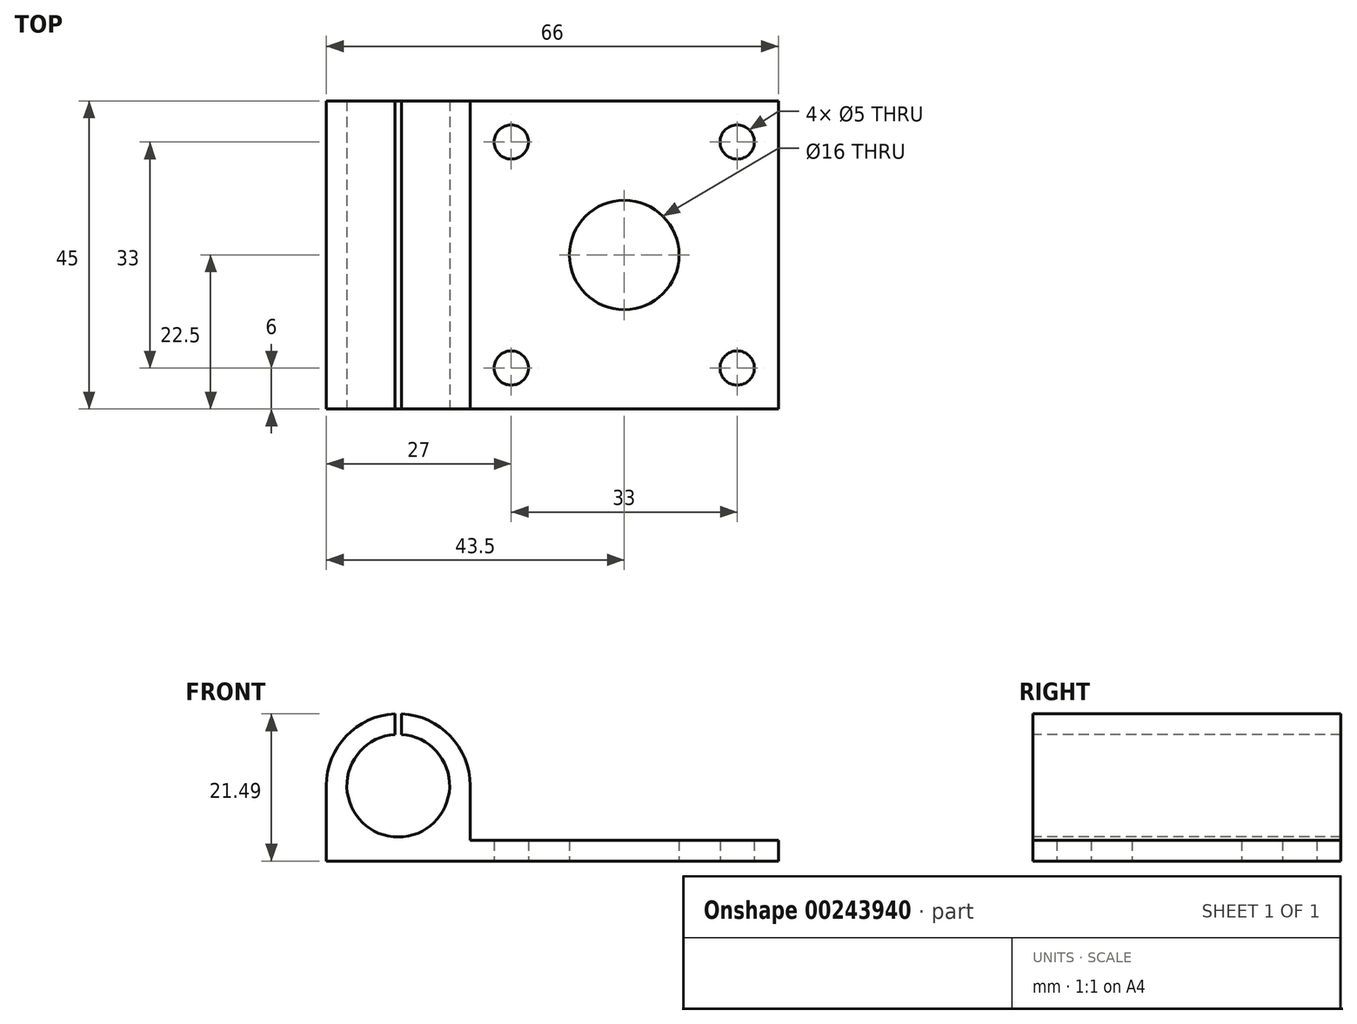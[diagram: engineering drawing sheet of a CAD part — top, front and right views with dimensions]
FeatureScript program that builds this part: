
annotation { "Feature Type Name" : "Feature", "Feature Type Description" : "" }
export const myFeature = defineFeature(function(context is Context, id is Id, definition is map)
    precondition{}
    {
        {
            var Q0;
            Q0=qCreatedBy(makeId("Front.planeOp"),FACE);
            var sketch = newSketch(context, id + "F0", { "sketchPlane" : qUnion([Q0])});
            skArc(sketch, "E0", {"start": v(-11, 18.48) * mm, "mid": v(-10.5, 3.5) * mm, "end": v(-10, 18.48) * mm});
            skArc(sketch, "E1", {"start": v(-11, 21.49) * mm, "mid": v(-18.1, 18.25) * mm, "end": v(-21, 11) * mm});
            skLineSegment(sketch, "E2.0", {"start": v(-21, 0) * mm, "end": v(-21, 11) * mm});
            skLineSegment(sketch, "E3.0", {"start": v(45, 3) * mm, "end": v(0, 3) * mm});
            skLineSegment(sketch, "E4.trimOffspring", {"start": v(-11, 18.48) * mm, "end": v(-11, 21.5) * mm});
            skLineSegment(sketch, "E5.trimOffspring", {"start": v(-10, 18.48) * mm, "end": v(-10, 21.5) * mm});
            skArc(sketch, "E6.trimOffspring", {"start": v(0, 11) * mm, "mid": v(-2.9, 18.25) * mm, "end": v(-10, 21.49) * mm});
            skLineSegment(sketch, "E7", {"start": v(-21, 0) * mm, "end": v(45, 0) * mm});
            skPoint(sketch, "E8.endSnap0", {"position": v(-10.5, 3.5) * mm});
            skLineSegment(sketch, "E9.0", {"start": v(0, 11) * mm, "end": v(0, 3) * mm});
            skLineSegment(sketch, "E10", {"start": v(0, 3) * mm, "end": v(0, 0) * mm, "construction": true});
            skLineSegment(sketch, "E11.0", {"start": v(45, 3) * mm, "end": v(45, 0) * mm});
            skSolve(sketch);
        }
        {
            var Q0;
            {var subQ1=sQuery(id+"F0.wireOp",EDGE,"E0");Q0=makeQuery(id+"F0.imprint","IMPRINT",FACE,{"disambiguationData":[TD([[makeQuery(id+"F0.imprint","IMPRINT",EDGE,{"derivedFrom":subQ1}),-1.0]])]});}
            extrude(context, id + "F1", {"entities" : qUnion([Q0]), "oppositeDirection" : true, "depth" : 45 * mm});
        }
        {
            var Q0;
            Q0=qCreatedBy(makeId("Top.planeOp"),FACE);
            var sketch = newSketch(context, id + "F2", { "sketchPlane" : qUnion([Q0])});
            skLineSegment(sketch, "E12", {"start": v(0, 0) * mm, "end": v(0, 22.5) * mm, "construction": true});
            skLineSegment(sketch, "E13", {"start": v(0, 22.5) * mm, "end": v(22.5, 22.5) * mm, "construction": true});
            skLineSegment(sketch, "E14", {"start": v(0, 0) * mm, "end": v(45, 0) * mm, "construction": true});
            skLineSegment(sketch, "E15", {"start": v(45, 0) * mm, "end": v(45, 45) * mm, "construction": true});
            skLineSegment(sketch, "E16", {"start": v(45, 45) * mm, "end": v(0, 45) * mm, "construction": true});
            skLineSegment(sketch, "E17.0", {"start": v(6, 6) * mm, "end": v(6, 39) * mm, "construction": true});
            skLineSegment(sketch, "E18.0", {"start": v(6, 6) * mm, "end": v(39, 6) * mm, "construction": true});
            skLineSegment(sketch, "E19.0", {"start": v(39, 6) * mm, "end": v(39, 39) * mm, "construction": true});
            skLineSegment(sketch, "E20.0", {"start": v(39, 39) * mm, "end": v(6, 39) * mm, "construction": true});
            skCircle(sketch, "E21", {"center": v(22.5, 22.5) * mm, "radius": 8 * mm});
            skCircle(sketch, "E22", {"center": v(6, 6) * mm, "radius": 2.5 * mm});
            skCircle(sketch, "E23", {"center": v(39, 6) * mm, "radius": 2.5 * mm});
            skCircle(sketch, "E24", {"center": v(6, 39) * mm, "radius": 2.5 * mm});
            skCircle(sketch, "E25", {"center": v(39, 39) * mm, "radius": 2.5 * mm});
            skSolve(sketch);
        }
        {
            var Q0;
            Q0=makeQuery(id+"F2.imprint","IMPRINT",FACE,{"disambiguationData":[TD([[makeQuery(id+"F2.imprint","IMPRINT",EDGE,{"derivedFrom":sQuery(id+"F2.wireOp",EDGE,"E21")}),1.0]])]});
            var Q1;
            Q1=makeQuery(id+"F2.imprint","IMPRINT",FACE,{"disambiguationData":[TD([[makeQuery(id+"F2.imprint","IMPRINT",EDGE,{"derivedFrom":sQuery(id+"F2.wireOp",EDGE,"E24")}),1.0]])]});
            var Q2;
            Q2=makeQuery(id+"F2.imprint","IMPRINT",FACE,{"disambiguationData":[TD([[makeQuery(id+"F2.imprint","IMPRINT",EDGE,{"derivedFrom":sQuery(id+"F2.wireOp",EDGE,"E25")}),1.0]])]});
            var Q3;
            Q3=makeQuery(id+"F2.imprint","IMPRINT",FACE,{"disambiguationData":[TD([[makeQuery(id+"F2.imprint","IMPRINT",EDGE,{"derivedFrom":sQuery(id+"F2.wireOp",EDGE,"E23")}),1.0]])]});
            var Q4;
            Q4=makeQuery(id+"F2.imprint","IMPRINT",FACE,{"disambiguationData":[TD([[makeQuery(id+"F2.imprint","IMPRINT",EDGE,{"derivedFrom":sQuery(id+"F2.wireOp",EDGE,"E22")}),1.0]])]});
            extrude(context, id + "F3", {"entities" : qUnion([Q0, Q1, Q2, Q3, Q4]), "operationType" : NewBodyOperationType.REMOVE, "depth" : 10 * mm});
        }
    });
